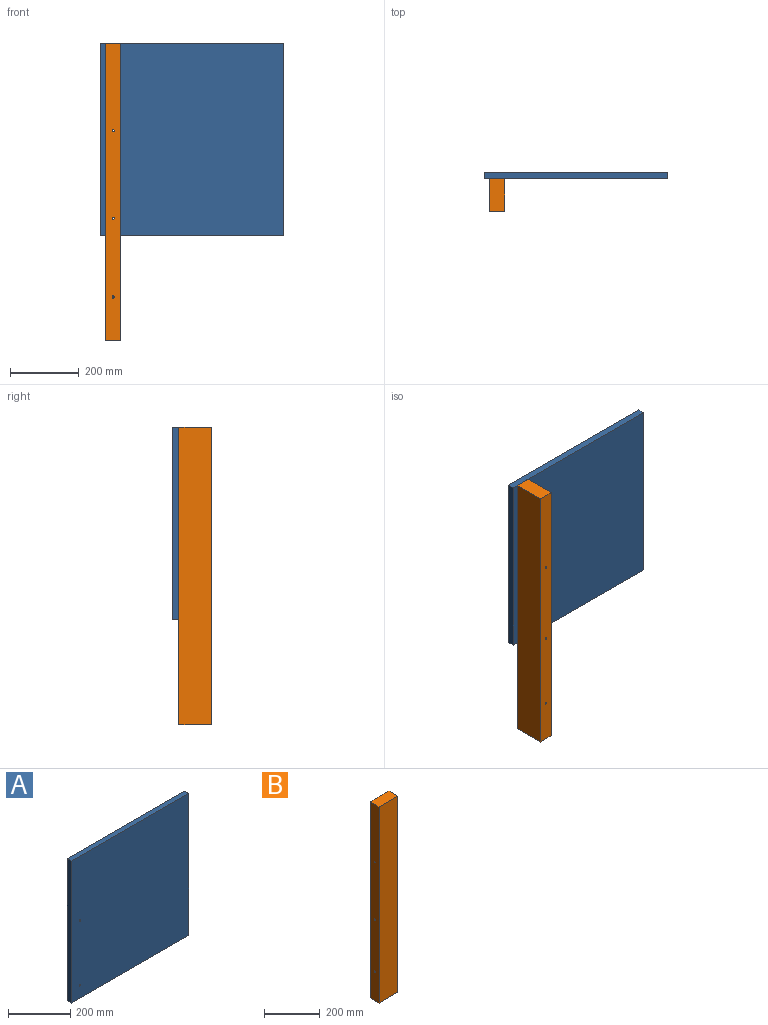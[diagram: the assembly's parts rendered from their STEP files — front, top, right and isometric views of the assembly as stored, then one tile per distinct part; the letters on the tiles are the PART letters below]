
ASSEMBLY  parts=2 mates=1
PART A: 8 faces, bbox 533.4x19.1x558.8 mm
  f0: plane 533.4x19.05mm, normal (0,0,1), area 10161.3mm2, adj f1,f3,f4,f5
  f1: plane 558.8x19.05mm, normal (-1,0,0), area 10645.1mm2, adj f0,f2,f4,f5
  f2: plane 533.4x19.05mm, normal (0,0,-1), area 10161.3mm2, adj f1,f3,f4,f5
  f3: plane 558.8x19.05mm, normal (1,0,0), area 10645.1mm2, adj f0,f2,f4,f5
  f4: plane 558.8x533.4mm, normal (0,-1,0), area 298000.6mm2, adj f0,f1,f2,f3,f6,f7
  f5: plane 558.8x533.4mm, normal (0,1,0), area 298000.6mm2, adj f0,f1,f2,f3,f6,f7
  f6: cylinder r=3.17mm len=19.05mm, axis (0,1,0), area 380mm2, adj f4,f5
  f7: cylinder r=3.17mm len=19.05mm, axis (0,1,0), area 380mm2, adj f4,f5
PART B: 9 faces, bbox 95.3x44.5x863.6 mm
  f0: plane 95.25x44.45mm, normal (0,0,1), area 4233.9mm2, adj f1,f3,f4,f5
  f1: plane 863.6x44.45mm, normal (-1,0,0), area 38292mm2, adj f0,f2,f4,f5,f6,f7,f8
  f2: plane 95.25x44.45mm, normal (0,0,-1), area 4233.9mm2, adj f1,f3,f4,f5
  f3: plane 863.6x44.45mm, normal (1,0,0), area 38292mm2, adj f0,f2,f4,f5,f6,f7,f8
  f4: plane 863.6x95.25mm, normal (0,-1,0), area 82257.9mm2, adj f0,f1,f2,f3
  f5: plane 863.6x95.25mm, normal (0,1,0), area 82257.9mm2, adj f0,f1,f2,f3
  f6: cylinder r=3.17mm len=95.25mm, axis (1,0,0), area 1900.2mm2, adj f1,f3
  f7: cylinder r=3.17mm len=95.25mm, axis (1,0,0), area 1900.2mm2, adj f1,f3
  f8: cylinder r=3.17mm len=95.25mm, axis (1,0,0), area 1900.2mm2, adj f1,f3
PLACE A t=(-395.12,-42.41,1381.16)mm
PLACE B rot(axis=(0,0,-1),90deg) t=(-868.19,-156.71,44.02)mm
MATE fastened B.f8 <-> A.f7  axis (0,1,0) through (-890.42,-61.46,254.53)mm
